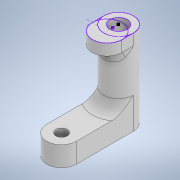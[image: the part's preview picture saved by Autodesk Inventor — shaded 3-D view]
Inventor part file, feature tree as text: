
AUTODESK INVENTOR PART (.ipt)
format: ipt  version: 2021.1 (Build 251245010, 245A)  size: 238,080 bytes
history: native  units: mm
features: extrude x4, sketch x3, other x2, fillet x2
ambient origin geometry x8: Origin, YZ Plane, XZ Plane, XY Plane, X Axis, Y Axis, Z Axis, Center Point
bodies: Volumenkörper1 (feature_tree)
feature tree (11):
  other  "OBS-M-003_v4"
  sketch  "Skizze1"  dims[d0=2.0mm d1=0.0mm d2=11.5mm d3=0.0mm]
  extrude  "Extrusion1"  Depth=2.0mm TaperAngle=0.0deg
  extrude  "Extrusion2"  Depth=2.0mm TaperAngle=0.0deg
  fillet  "Rundung1"  Radius=2.0mm
  extrude  "Extrusion3"  Depth=10.0mm TaperAngle=0.0deg
  fillet  "Rundung2"  [1 undecoded]
  extrude  "Extrusion4"  [1 undecoded]
  sketch  "Skizze2"  dims[d4=2.0mm d6=3.5mm d7=0.0mm d8=2.0mm]
  sketch  "Skizze3"  dims[d9=2.0mm d10=10.0mm d11=0.0mm]
  other  "MeshFeature1"
note: 2 required parameter values undecoded (feature->parameter linkage not recoverable at this tier; creation-order binding heuristic only, values carry confidence <= 0.55)
